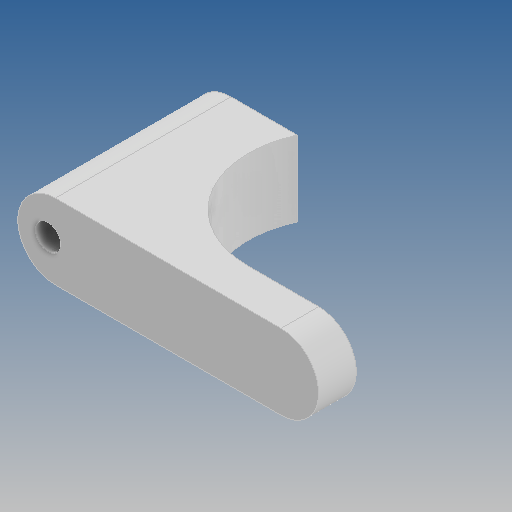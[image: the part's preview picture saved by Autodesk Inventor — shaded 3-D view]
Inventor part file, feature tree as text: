
AUTODESK INVENTOR PART (.ipt)
format: ipt  version: 2020 (Build 240168000, 168)  size: 120,832 bytes
history: native  units: mm
features: extrude x2, sketch x2, other x2, fillet x1, reference x1
ambient origin geometry x8: Origin, YZ Plane, XZ Plane, XY Plane, X Axis, Y Axis, Z Axis, Center Point
bodies: Solid1 (feature_tree)
feature tree (8):
  extrude  "Extrusion1"  Depth=6.0mm
  extrude  "Extrusion2"  Depth=7.5mm
  fillet  "Fillet1"  Radius=35.0mm
  sketch  "Sketch1"  dims[d0=5.0mm d1=6.0mm]
  sketch  "Sketch2"  dims[d2=15.0mm d3=60.0mm d4=35.0mm d5=0.0mm d6=39.0mm d7=0.0mm d8=0.0mm d9=7.5mm d10=0.872665mm]
  reference  "Reference1"
  other  "30-00 Injectomat suplimentar.iam"
  other  "Corp:2"
